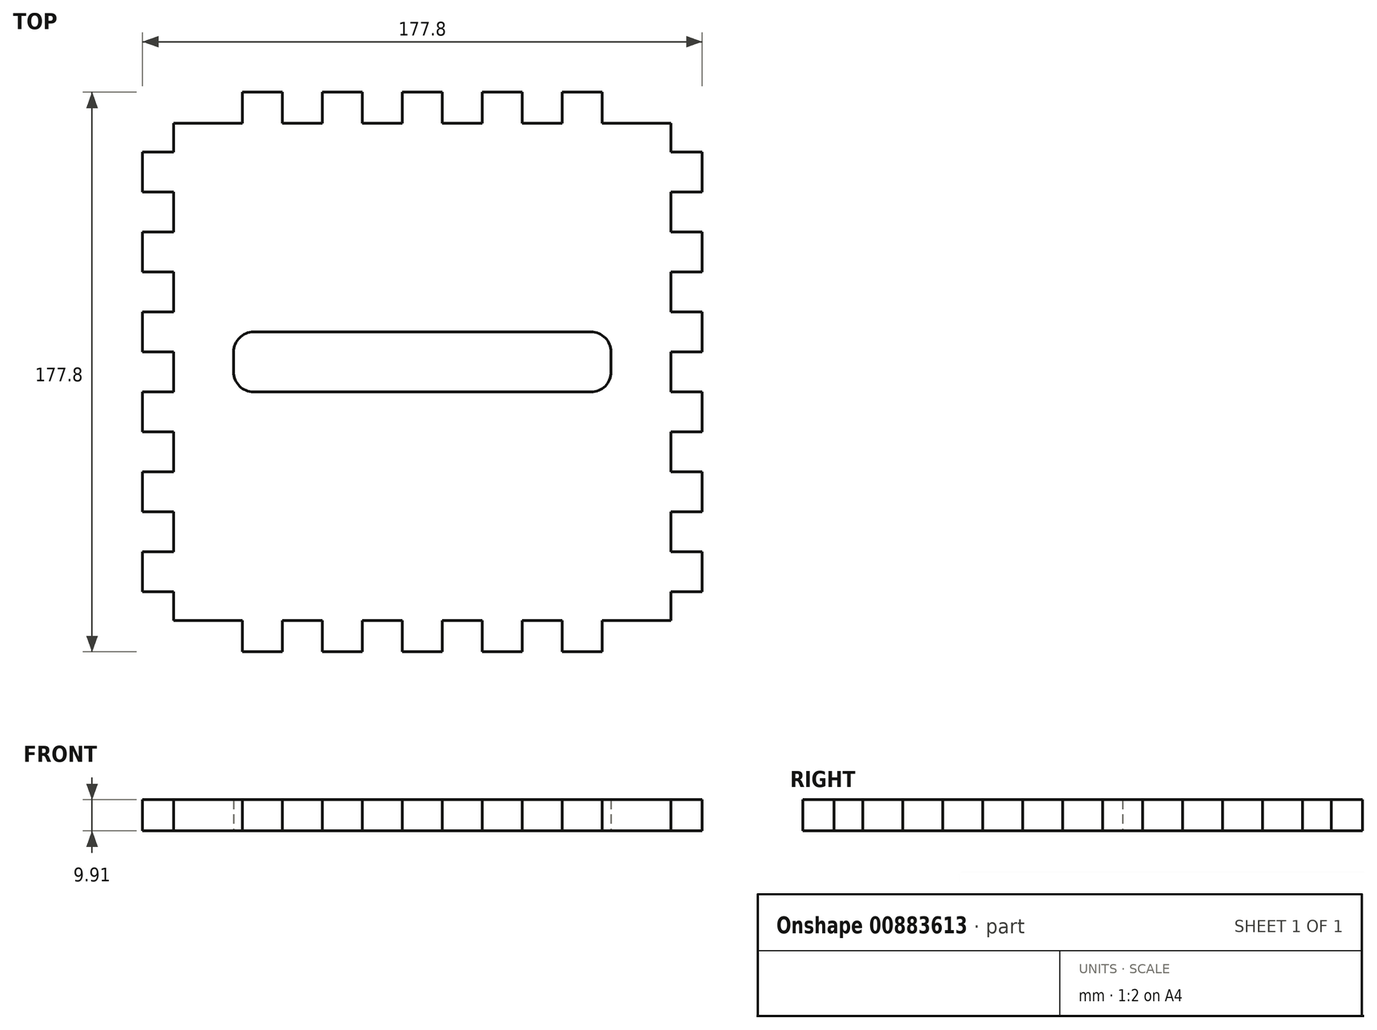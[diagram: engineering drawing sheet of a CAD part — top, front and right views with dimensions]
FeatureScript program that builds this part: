
annotation { "Feature Type Name" : "Feature", "Feature Type Description" : "" }
export const myFeature = defineFeature(function(context is Context, id is Id, definition is map)
    precondition{}
    {
        {
            var Q0;
            Q0=qCreatedBy(makeId("Top.planeOp"),FACE);
            var sketch = newSketch(context, id + "F0", { "sketchPlane" : qUnion([Q0])});
            skLineSegment(sketch, "E0.bottom", {"start": v(31.75, 0) * mm, "end": v(44.45, 0) * mm});
            skLineSegment(sketch, "E0.left", {"start": v(0, -19.05) * mm, "end": v(0, -31.75) * mm});
            skLineSegment(sketch, "E1", {"start": v(0, -19.05) * mm, "end": v(9.9, -19.05) * mm});
            skLineSegment(sketch, "E2", {"start": v(9.9, -9.9) * mm, "end": v(31.75, -9.9) * mm});
            skLineSegment(sketch, "E3", {"start": v(31.75, -9.9) * mm, "end": v(31.75, 0) * mm});
            skLineSegment(sketch, "E4", {"start": v(9.9, -19.05) * mm, "end": v(9.9, -9.9) * mm});
            skPoint(sketch, "E5.orphan", {"position": v(0, 0) * mm});
            skLineSegment(sketch, "E6", {"start": v(44.45, 0) * mm, "end": v(44.45, -9.9) * mm});
            skLineSegment(sketch, "E7", {"start": v(44.45, -9.9) * mm, "end": v(57.15, -9.9) * mm});
            skLineSegment(sketch, "E8", {"start": v(57.15, -9.9) * mm, "end": v(57.15, 0) * mm});
            skLineSegment(sketch, "E9", {"start": v(57.15, 0) * mm, "end": v(69.85, 0) * mm});
            skLineSegment(sketch, "E10", {"start": v(69.85, 0) * mm, "end": v(69.85, -9.9) * mm});
            skLineSegment(sketch, "E11", {"start": v(69.85, -9.9) * mm, "end": v(82.55, -9.9) * mm});
            skLineSegment(sketch, "E12", {"start": v(82.55, -9.9) * mm, "end": v(82.55, 0) * mm});
            skLineSegment(sketch, "E13", {"start": v(82.55, 0) * mm, "end": v(95.25, 0) * mm});
            skLineSegment(sketch, "E14", {"start": v(95.25, 0) * mm, "end": v(95.25, -9.9) * mm});
            skLineSegment(sketch, "E15", {"start": v(95.25, -9.9) * mm, "end": v(107.95, -9.9) * mm});
            skLineSegment(sketch, "E16", {"start": v(107.95, -9.9) * mm, "end": v(107.95, 0) * mm});
            skLineSegment(sketch, "E17.trimOffspring", {"start": v(107.95, 0) * mm, "end": v(120.65, 0) * mm});
            skLineSegment(sketch, "E18", {"start": v(120.65, 0) * mm, "end": v(120.65, -9.9) * mm});
            skLineSegment(sketch, "E19", {"start": v(120.65, -9.9) * mm, "end": v(133.35, -9.9) * mm});
            skLineSegment(sketch, "E20", {"start": v(133.35, -9.9) * mm, "end": v(133.35, 0) * mm});
            skLineSegment(sketch, "E21", {"start": v(133.35, 0) * mm, "end": v(146.05, 0) * mm});
            skLineSegment(sketch, "E22", {"start": v(146.05, 0) * mm, "end": v(146.05, -9.9) * mm});
            skLineSegment(sketch, "E23", {"start": v(146.05, -9.9) * mm, "end": v(167.9, -9.9) * mm});
            skLineSegment(sketch, "E24", {"start": v(167.9, -9.9) * mm, "end": v(167.9, -19.05) * mm});
            skLineSegment(sketch, "E25", {"start": v(167.9, -19.05) * mm, "end": v(177.8, -19.05) * mm});
            skPoint(sketch, "E26.orphan", {"position": v(177.8, 0) * mm});
            skLineSegment(sketch, "E27", {"start": v(0, -31.75) * mm, "end": v(9.9, -31.75) * mm});
            skLineSegment(sketch, "E28", {"start": v(9.9, -31.75) * mm, "end": v(9.9, -44.45) * mm});
            skLineSegment(sketch, "E29", {"start": v(9.9, -44.45) * mm, "end": v(0, -44.45) * mm});
            skLineSegment(sketch, "E30", {"start": v(0, -44.45) * mm, "end": v(0, -57.15) * mm});
            skLineSegment(sketch, "E31", {"start": v(0, -57.15) * mm, "end": v(9.9, -57.15) * mm});
            skLineSegment(sketch, "E32", {"start": v(9.9, -57.15) * mm, "end": v(9.9, -69.85) * mm});
            skLineSegment(sketch, "E33", {"start": v(9.9, -69.85) * mm, "end": v(0, -69.85) * mm});
            skLineSegment(sketch, "E34", {"start": v(0, -69.85) * mm, "end": v(0, -82.55) * mm});
            skLineSegment(sketch, "E35", {"start": v(0, -82.55) * mm, "end": v(9.9, -82.55) * mm});
            skLineSegment(sketch, "E36", {"start": v(9.9, -82.55) * mm, "end": v(9.9, -95.25) * mm});
            skLineSegment(sketch, "E37", {"start": v(9.9, -95.25) * mm, "end": v(0, -95.25) * mm});
            skLineSegment(sketch, "E38.trimOffspring", {"start": v(0, -95.25) * mm, "end": v(0, -107.95) * mm});
            skLineSegment(sketch, "E39", {"start": v(0, -107.95) * mm, "end": v(9.9, -107.95) * mm});
            skLineSegment(sketch, "E40", {"start": v(9.9, -107.95) * mm, "end": v(9.9, -120.65) * mm});
            skLineSegment(sketch, "E41", {"start": v(9.9, -120.65) * mm, "end": v(0, -120.65) * mm});
            skLineSegment(sketch, "E42", {"start": v(0, -120.65) * mm, "end": v(0, -133.35) * mm});
            skLineSegment(sketch, "E43", {"start": v(0, -133.35) * mm, "end": v(9.9, -133.35) * mm});
            skLineSegment(sketch, "E44", {"start": v(9.9, -133.35) * mm, "end": v(9.9, -146.05) * mm});
            skLineSegment(sketch, "E45", {"start": v(9.9, -146.05) * mm, "end": v(0, -146.05) * mm});
            skLineSegment(sketch, "E46.trimOffspring", {"start": v(0, -146.05) * mm, "end": v(0, -158.75) * mm});
            skLineSegment(sketch, "E47", {"start": v(0, -158.75) * mm, "end": v(9.9, -158.75) * mm});
            skLineSegment(sketch, "E48", {"start": v(9.9, -158.75) * mm, "end": v(9.9, -167.9) * mm});
            skPoint(sketch, "E49.orphan", {"position": v(0, -177.8) * mm});
            skLineSegment(sketch, "E50", {"start": v(88.9, 0) * mm, "end": v(88.9, -25.4) * mm, "construction": true});
            skLineSegment(sketch, "E51", {"start": v(9.9, -88.9) * mm, "end": v(35.3, -88.9) * mm, "construction": true});
            skLineSegment(sketch, "E52.MirrorCS", {"start": v(177.8, -44.45) * mm, "end": v(177.8, -57.15) * mm});
            skLineSegment(sketch, "E53.MirrorCS", {"start": v(177.8, -57.15) * mm, "end": v(167.9, -57.15) * mm});
            skLineSegment(sketch, "E54.MirrorCS", {"start": v(167.9, -158.75) * mm, "end": v(167.9, -167.9) * mm});
            skLineSegment(sketch, "E55.MirrorCS", {"start": v(177.8, -133.35) * mm, "end": v(167.9, -133.35) * mm});
            skLineSegment(sketch, "E56.MirrorCS", {"start": v(177.8, -107.95) * mm, "end": v(167.9, -107.95) * mm});
            skLineSegment(sketch, "E57.MirrorCS", {"start": v(167.9, -120.65) * mm, "end": v(177.8, -120.65) * mm});
            skLineSegment(sketch, "E58.MirrorCS", {"start": v(167.9, -69.85) * mm, "end": v(177.8, -69.85) * mm});
            skLineSegment(sketch, "E59.MirrorCS", {"start": v(177.8, -31.75) * mm, "end": v(167.9, -31.75) * mm});
            skLineSegment(sketch, "E60.MirrorCS", {"start": v(167.9, -146.05) * mm, "end": v(177.8, -146.05) * mm});
            skLineSegment(sketch, "E61.MirrorCS", {"start": v(167.9, -44.45) * mm, "end": v(177.8, -44.45) * mm});
            skLineSegment(sketch, "E62.MirrorCS", {"start": v(177.8, -158.75) * mm, "end": v(167.9, -158.75) * mm});
            skLineSegment(sketch, "E63.MirrorCS", {"start": v(177.8, -82.55) * mm, "end": v(167.9, -82.55) * mm});
            skLineSegment(sketch, "E64.MirrorCS", {"start": v(167.9, -95.25) * mm, "end": v(177.8, -95.25) * mm});
            skLineSegment(sketch, "E65.MirrorCS", {"start": v(177.8, -69.85) * mm, "end": v(177.8, -82.55) * mm});
            skLineSegment(sketch, "E66.MirrorCS", {"start": v(177.8, -146.05) * mm, "end": v(177.8, -158.75) * mm});
            skLineSegment(sketch, "E67.MirrorCS", {"start": v(167.9, -82.55) * mm, "end": v(167.9, -95.25) * mm});
            skLineSegment(sketch, "E68.MirrorCS", {"start": v(177.8, -95.25) * mm, "end": v(177.8, -107.95) * mm});
            skLineSegment(sketch, "E69.MirrorCS", {"start": v(177.8, -120.65) * mm, "end": v(177.8, -133.35) * mm});
            skLineSegment(sketch, "E70.MirrorCS", {"start": v(167.9, -57.15) * mm, "end": v(167.9, -69.85) * mm});
            skLineSegment(sketch, "E71.MirrorCS", {"start": v(167.9, -133.35) * mm, "end": v(167.9, -146.05) * mm});
            skLineSegment(sketch, "E72.MirrorCS", {"start": v(167.9, -31.75) * mm, "end": v(167.9, -44.45) * mm});
            skLineSegment(sketch, "E73.MirrorCS", {"start": v(167.9, -107.95) * mm, "end": v(167.9, -120.65) * mm});
            skLineSegment(sketch, "E74.MirrorCS", {"start": v(177.8, -19.05) * mm, "end": v(177.8, -31.75) * mm});
            skLineSegment(sketch, "E75.MirrorCS", {"start": v(120.65, -177.8) * mm, "end": v(120.65, -167.9) * mm});
            skLineSegment(sketch, "E76.MirrorCS", {"start": v(95.25, -177.8) * mm, "end": v(95.25, -167.9) * mm});
            skLineSegment(sketch, "E77.MirrorCS", {"start": v(82.55, -167.9) * mm, "end": v(82.55, -177.8) * mm});
            skLineSegment(sketch, "E78.MirrorCS", {"start": v(57.15, -167.9) * mm, "end": v(57.15, -177.8) * mm});
            skLineSegment(sketch, "E79.MirrorCS", {"start": v(133.35, -167.9) * mm, "end": v(133.35, -177.8) * mm});
            skLineSegment(sketch, "E80.MirrorCS", {"start": v(146.05, -177.8) * mm, "end": v(146.05, -167.9) * mm});
            skLineSegment(sketch, "E81.MirrorCS", {"start": v(44.45, -177.8) * mm, "end": v(44.45, -167.9) * mm});
            skLineSegment(sketch, "E82.MirrorCS", {"start": v(107.95, -167.9) * mm, "end": v(107.95, -177.8) * mm});
            skLineSegment(sketch, "E83.MirrorCS", {"start": v(69.85, -177.8) * mm, "end": v(69.85, -167.9) * mm});
            skLineSegment(sketch, "E84.MirrorCS", {"start": v(82.55, -177.8) * mm, "end": v(95.25, -177.8) * mm});
            skLineSegment(sketch, "E85.MirrorCS", {"start": v(31.75, -167.9) * mm, "end": v(31.75, -177.8) * mm});
            skLineSegment(sketch, "E86.MirrorCS", {"start": v(133.35, -177.8) * mm, "end": v(146.05, -177.8) * mm});
            skLineSegment(sketch, "E87.MirrorCS", {"start": v(107.95, -177.8) * mm, "end": v(120.65, -177.8) * mm});
            skLineSegment(sketch, "E88.MirrorCS", {"start": v(57.15, -177.8) * mm, "end": v(69.85, -177.8) * mm});
            skLineSegment(sketch, "E89.MirrorCS", {"start": v(31.75, -177.8) * mm, "end": v(44.45, -177.8) * mm});
            skLineSegment(sketch, "E90.MirrorCS", {"start": v(120.65, -167.9) * mm, "end": v(133.35, -167.9) * mm});
            skLineSegment(sketch, "E91.MirrorCS", {"start": v(44.45, -167.9) * mm, "end": v(57.15, -167.9) * mm});
            skLineSegment(sketch, "E92.MirrorCS", {"start": v(95.25, -167.9) * mm, "end": v(107.95, -167.9) * mm});
            skLineSegment(sketch, "E93.MirrorCS", {"start": v(69.85, -167.9) * mm, "end": v(82.55, -167.9) * mm});
            skLineSegment(sketch, "E94.MirrorCS", {"start": v(9.9, -167.9) * mm, "end": v(31.75, -167.9) * mm});
            skLineSegment(sketch, "E95.MirrorCS", {"start": v(146.05, -167.9) * mm, "end": v(167.9, -167.9) * mm});
            skLineSegment(sketch, "E96.bottom", {"start": v(35.3, -76.2) * mm, "end": v(142.5, -76.2) * mm});
            skLineSegment(sketch, "E96.top", {"start": v(35.3, -95.25) * mm, "end": v(142.5, -95.25) * mm});
            skLineSegment(sketch, "E96.left", {"start": v(28.96, -82.55) * mm, "end": v(28.96, -88.9) * mm});
            skLineSegment(sketch, "E96.right", {"start": v(148.84, -82.55) * mm, "end": v(148.84, -88.9) * mm});
            skPoint(sketch, "E97.visualSharp", {"position": v(28.96, -76.2) * mm});
            skArc(sketch, "E97.filletArc", {"start": v(35.3, -76.2) * mm, "mid": v(30.82, -78.06) * mm, "end": v(28.96, -82.55) * mm});
            skPoint(sketch, "E98.visualSharp", {"position": v(28.96, -95.25) * mm});
            skArc(sketch, "E98.filletArc", {"start": v(28.96, -88.9) * mm, "mid": v(30.82, -93.4) * mm, "end": v(35.3, -95.25) * mm});
            skPoint(sketch, "E99.visualSharp", {"position": v(148.84, -76.2) * mm});
            skArc(sketch, "E99.filletArc", {"start": v(148.84, -82.55) * mm, "mid": v(146.98, -78.06) * mm, "end": v(142.5, -76.2) * mm});
            skPoint(sketch, "E100.visualSharp", {"position": v(148.84, -95.25) * mm});
            skArc(sketch, "E100.filletArc", {"start": v(142.5, -95.25) * mm, "mid": v(146.98, -93.4) * mm, "end": v(148.84, -88.9) * mm});
            skSolve(sketch);
        }
        {
            var Q0;
            Q0=makeQuery(id+"F0.imprint","IMPRINT",FACE,{"disambiguationData":[TD([[makeQuery(id+"F0.imprint","IMPRINT",EDGE,{"derivedFrom":sQuery(id+"F0.wireOp",EDGE,"E1")}),-1.0]])]});
            extrude(context, id + "F1", {"entities" : qUnion([Q0]), "depth" : 9.9 * mm, "offsetDistance" : 25.4 * mm});
        }
        {
            var Q0;
            Q0=makeQuery(id+"F0.imprint","IMPRINT",FACE,{"disambiguationData":[TD([[makeQuery(id+"F0.imprint","IMPRINT",EDGE,{"derivedFrom":sQuery(id+"F0.wireOp",EDGE,"E32")}),1.0]])]});
            extrude(context, id + "F2", {"entities" : qUnion([Q0]), "depth" : 9.9 * mm, "offsetDistance" : 25.4 * mm});
        }
    });
